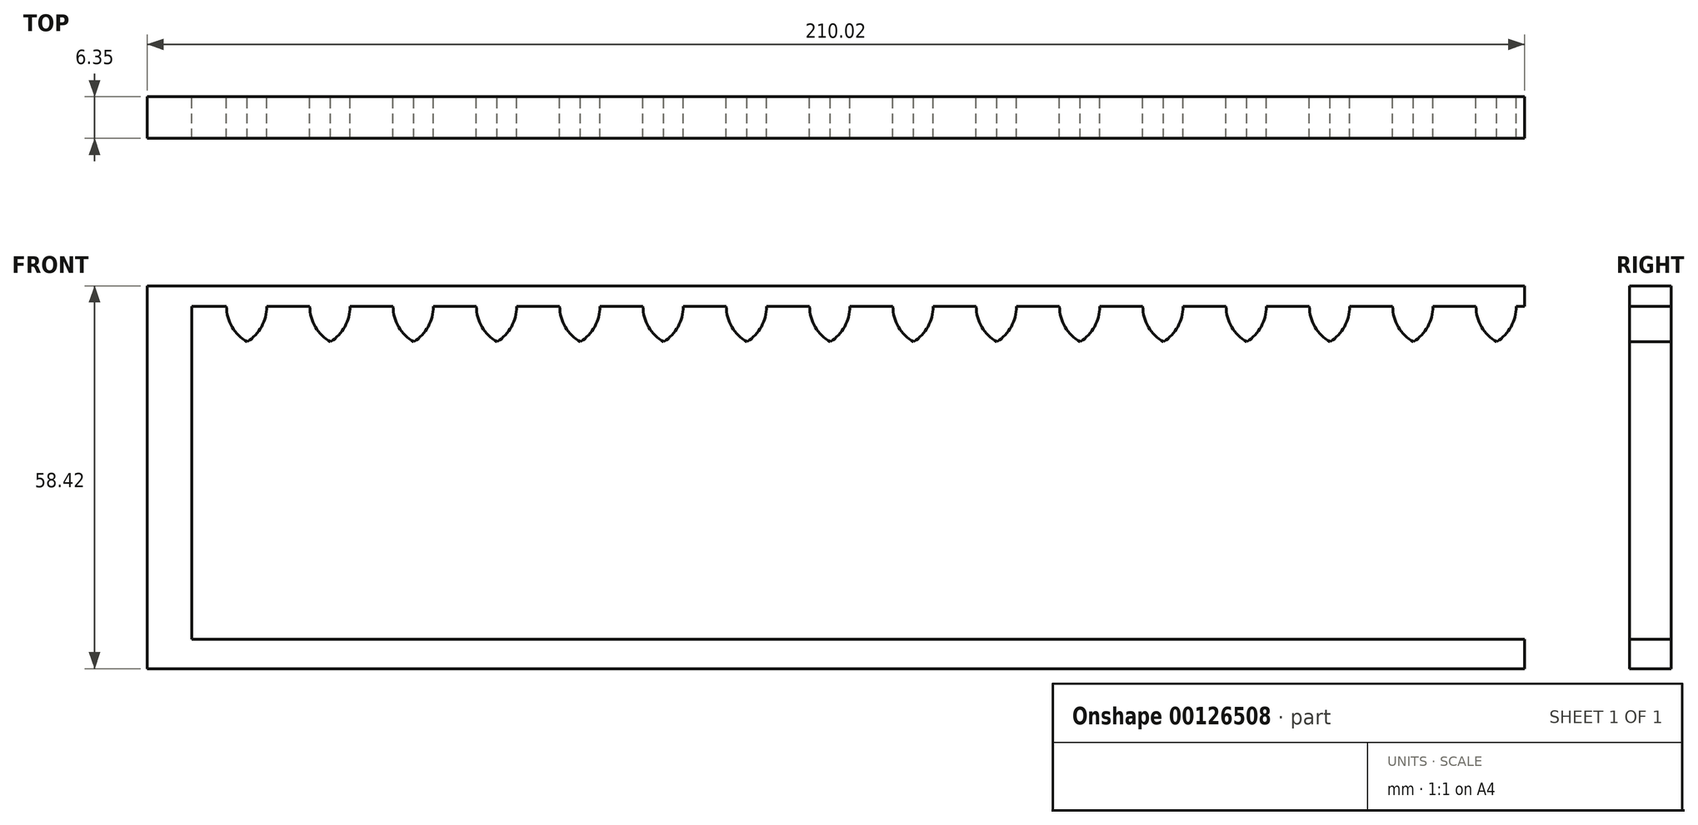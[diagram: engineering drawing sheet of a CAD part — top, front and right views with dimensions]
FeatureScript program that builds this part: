
annotation { "Feature Type Name" : "Feature", "Feature Type Description" : "" }
export const myFeature = defineFeature(function(context is Context, id is Id, definition is map)
    precondition{}
    {
        {
            var Q0;
            Q0=qCreatedBy(makeId("Front.planeOp"),FACE);
            var sketch = newSketch(context, id + "F0", { "sketchPlane" : qUnion([Q0])});
            skLineSegment(sketch, "E0.bottom", {"start": v(-100.17, 36.3) * mm, "end": v(103.03, 36.3) * mm});
            skLineSegment(sketch, "E0.top", {"start": v(-100.17, -14.5) * mm, "end": v(103.03, -14.5) * mm});
            skLineSegment(sketch, "E0.left", {"start": v(-100.17, 36.3) * mm, "end": v(-100.17, -14.5) * mm});
            skArc(sketch, "E1", {"start": v(-91.7, 30.93) * mm, "mid": v(-89.52, 33.23) * mm, "end": v(-88.73, 36.3) * mm});
            skArc(sketch, "E2", {"start": v(-94.87, 36.3) * mm, "mid": v(-94.02, 33.18) * mm, "end": v(-91.7, 30.93) * mm});
            skArc(sketch, "E3.1.0.0", {"start": v(-79, 30.93) * mm, "mid": v(-76.82, 33.23) * mm, "end": v(-76.03, 36.3) * mm});
            skArc(sketch, "E3.1.0.1", {"start": v(-82.17, 36.3) * mm, "mid": v(-81.32, 33.18) * mm, "end": v(-79, 30.93) * mm});
            skArc(sketch, "E3.2.0.0", {"start": v(-66.3, 30.93) * mm, "mid": v(-64.12, 33.23) * mm, "end": v(-63.33, 36.3) * mm});
            skArc(sketch, "E3.2.0.1", {"start": v(-69.47, 36.3) * mm, "mid": v(-68.62, 33.18) * mm, "end": v(-66.3, 30.93) * mm});
            skArc(sketch, "E3.3.0.0", {"start": v(-53.6, 30.93) * mm, "mid": v(-51.42, 33.23) * mm, "end": v(-50.63, 36.3) * mm});
            skArc(sketch, "E3.3.0.1", {"start": v(-56.77, 36.3) * mm, "mid": v(-55.92, 33.18) * mm, "end": v(-53.6, 30.93) * mm});
            skArc(sketch, "E3.4.0.0", {"start": v(-40.9, 30.93) * mm, "mid": v(-38.72, 33.23) * mm, "end": v(-37.93, 36.3) * mm});
            skArc(sketch, "E3.4.0.1", {"start": v(-44.07, 36.3) * mm, "mid": v(-43.22, 33.18) * mm, "end": v(-40.9, 30.93) * mm});
            skArc(sketch, "E3.5.0.0", {"start": v(-28.2, 30.93) * mm, "mid": v(-26.02, 33.23) * mm, "end": v(-25.23, 36.3) * mm});
            skArc(sketch, "E3.5.0.1", {"start": v(-31.37, 36.3) * mm, "mid": v(-30.52, 33.18) * mm, "end": v(-28.2, 30.93) * mm});
            skArc(sketch, "E3.6.0.0", {"start": v(-15.5, 30.93) * mm, "mid": v(-13.32, 33.23) * mm, "end": v(-12.53, 36.3) * mm});
            skArc(sketch, "E3.6.0.1", {"start": v(-18.67, 36.3) * mm, "mid": v(-17.82, 33.18) * mm, "end": v(-15.5, 30.93) * mm});
            skArc(sketch, "E3.7.0.0", {"start": v(-2.8, 30.93) * mm, "mid": v(-0.62, 33.23) * mm, "end": v(0.17, 36.3) * mm});
            skArc(sketch, "E3.7.0.1", {"start": v(-5.97, 36.3) * mm, "mid": v(-5.12, 33.18) * mm, "end": v(-2.8, 30.93) * mm});
            skArc(sketch, "E3.8.0.0", {"start": v(9.9, 30.93) * mm, "mid": v(12.08, 33.23) * mm, "end": v(12.87, 36.3) * mm});
            skArc(sketch, "E3.8.0.1", {"start": v(6.73, 36.3) * mm, "mid": v(7.58, 33.18) * mm, "end": v(9.9, 30.93) * mm});
            skArc(sketch, "E3.9.0.0", {"start": v(22.6, 30.93) * mm, "mid": v(24.78, 33.23) * mm, "end": v(25.57, 36.3) * mm});
            skArc(sketch, "E3.9.0.1", {"start": v(19.43, 36.3) * mm, "mid": v(20.28, 33.18) * mm, "end": v(22.6, 30.93) * mm});
            skArc(sketch, "E3.10.0.0", {"start": v(35.3, 30.93) * mm, "mid": v(37.48, 33.23) * mm, "end": v(38.27, 36.3) * mm});
            skArc(sketch, "E3.10.0.1", {"start": v(32.13, 36.3) * mm, "mid": v(32.98, 33.18) * mm, "end": v(35.3, 30.93) * mm});
            skArc(sketch, "E3.11.0.0", {"start": v(48, 30.93) * mm, "mid": v(50.18, 33.23) * mm, "end": v(50.97, 36.3) * mm});
            skArc(sketch, "E3.11.0.1", {"start": v(44.83, 36.3) * mm, "mid": v(45.68, 33.18) * mm, "end": v(48, 30.93) * mm});
            skArc(sketch, "E3.12.0.0", {"start": v(60.7, 30.93) * mm, "mid": v(62.88, 33.23) * mm, "end": v(63.67, 36.3) * mm});
            skArc(sketch, "E3.12.0.1", {"start": v(57.53, 36.3) * mm, "mid": v(58.38, 33.18) * mm, "end": v(60.7, 30.93) * mm});
            skArc(sketch, "E3.13.0.0", {"start": v(73.4, 30.93) * mm, "mid": v(75.58, 33.23) * mm, "end": v(76.37, 36.3) * mm});
            skArc(sketch, "E3.13.0.1", {"start": v(70.23, 36.3) * mm, "mid": v(71.08, 33.18) * mm, "end": v(73.4, 30.93) * mm});
            skArc(sketch, "E3.14.0.0", {"start": v(86.1, 30.93) * mm, "mid": v(88.28, 33.23) * mm, "end": v(89.07, 36.3) * mm});
            skArc(sketch, "E3.14.0.1", {"start": v(82.93, 36.3) * mm, "mid": v(83.78, 33.18) * mm, "end": v(86.1, 30.93) * mm});
            skArc(sketch, "E3.15.0.0", {"start": v(98.8, 30.93) * mm, "mid": v(100.98, 33.23) * mm, "end": v(101.77, 36.3) * mm});
            skArc(sketch, "E3.15.0.1", {"start": v(95.63, 36.3) * mm, "mid": v(96.48, 33.18) * mm, "end": v(98.8, 30.93) * mm});
            skLineSegment(sketch, "E3.direction1", {"start": v(-91.7, 30.93) * mm, "end": v(-79, 30.93) * mm, "construction": true});
            skArc(sketch, "E4.MirrorCS", {"start": v(-94.87, -14.5) * mm, "mid": v(-94.02, -11.38) * mm, "end": v(-91.7, -9.13) * mm});
            skArc(sketch, "E5.MirrorCS", {"start": v(-91.7, -9.13) * mm, "mid": v(-89.52, -11.43) * mm, "end": v(-88.73, -14.5) * mm});
            skArc(sketch, "E6.MirrorCS", {"start": v(-82.17, -14.5) * mm, "mid": v(-81.32, -11.38) * mm, "end": v(-79, -9.13) * mm});
            skArc(sketch, "E7.MirrorCS", {"start": v(-79, -9.13) * mm, "mid": v(-76.82, -11.43) * mm, "end": v(-76.03, -14.5) * mm});
            skArc(sketch, "E8.MirrorCS", {"start": v(-69.47, -14.5) * mm, "mid": v(-68.62, -11.38) * mm, "end": v(-66.3, -9.13) * mm});
            skArc(sketch, "E9.MirrorCS", {"start": v(-66.3, -9.13) * mm, "mid": v(-64.12, -11.43) * mm, "end": v(-63.33, -14.5) * mm});
            skArc(sketch, "E10.MirrorCS", {"start": v(-56.77, -14.5) * mm, "mid": v(-55.92, -11.38) * mm, "end": v(-53.6, -9.13) * mm});
            skArc(sketch, "E11.MirrorCS", {"start": v(-53.6, -9.13) * mm, "mid": v(-51.42, -11.43) * mm, "end": v(-50.63, -14.5) * mm});
            skArc(sketch, "E12.MirrorCS", {"start": v(-44.07, -14.5) * mm, "mid": v(-43.22, -11.38) * mm, "end": v(-40.9, -9.13) * mm});
            skArc(sketch, "E13.MirrorCS", {"start": v(-40.9, -9.13) * mm, "mid": v(-38.72, -11.43) * mm, "end": v(-37.93, -14.5) * mm});
            skArc(sketch, "E14.MirrorCS", {"start": v(-31.37, -14.5) * mm, "mid": v(-30.52, -11.38) * mm, "end": v(-28.2, -9.13) * mm});
            skArc(sketch, "E15.MirrorCS", {"start": v(-28.2, -9.13) * mm, "mid": v(-26.02, -11.43) * mm, "end": v(-25.23, -14.5) * mm});
            skArc(sketch, "E16.MirrorCS", {"start": v(-18.67, -14.5) * mm, "mid": v(-17.82, -11.38) * mm, "end": v(-15.5, -9.13) * mm});
            skArc(sketch, "E17.MirrorCS", {"start": v(-15.5, -9.13) * mm, "mid": v(-13.32, -11.43) * mm, "end": v(-12.53, -14.5) * mm});
            skArc(sketch, "E18.MirrorCS", {"start": v(-5.97, -14.5) * mm, "mid": v(-5.12, -11.38) * mm, "end": v(-2.8, -9.13) * mm});
            skArc(sketch, "E19.MirrorCS", {"start": v(-2.8, -9.13) * mm, "mid": v(-0.62, -11.43) * mm, "end": v(0.17, -14.5) * mm});
            skArc(sketch, "E20.MirrorCS", {"start": v(6.73, -14.5) * mm, "mid": v(7.58, -11.38) * mm, "end": v(9.9, -9.13) * mm});
            skArc(sketch, "E21.MirrorCS", {"start": v(9.9, -9.13) * mm, "mid": v(12.08, -11.43) * mm, "end": v(12.87, -14.5) * mm});
            skArc(sketch, "E22.MirrorCS", {"start": v(19.43, -14.5) * mm, "mid": v(20.28, -11.38) * mm, "end": v(22.6, -9.13) * mm});
            skArc(sketch, "E23.MirrorCS", {"start": v(22.6, -9.13) * mm, "mid": v(24.78, -11.43) * mm, "end": v(25.57, -14.5) * mm});
            skArc(sketch, "E24.MirrorCS", {"start": v(32.13, -14.5) * mm, "mid": v(32.98, -11.38) * mm, "end": v(35.3, -9.13) * mm});
            skArc(sketch, "E25.MirrorCS", {"start": v(35.3, -9.13) * mm, "mid": v(37.48, -11.43) * mm, "end": v(38.27, -14.5) * mm});
            skArc(sketch, "E26.MirrorCS", {"start": v(44.83, -14.5) * mm, "mid": v(45.68, -11.38) * mm, "end": v(48, -9.13) * mm});
            skArc(sketch, "E27.MirrorCS", {"start": v(48, -9.13) * mm, "mid": v(50.18, -11.43) * mm, "end": v(50.97, -14.5) * mm});
            skArc(sketch, "E28.MirrorCS", {"start": v(57.53, -14.5) * mm, "mid": v(58.38, -11.38) * mm, "end": v(60.7, -9.13) * mm});
            skArc(sketch, "E29.MirrorCS", {"start": v(60.7, -9.13) * mm, "mid": v(62.88, -11.43) * mm, "end": v(63.67, -14.5) * mm});
            skArc(sketch, "E30.MirrorCS", {"start": v(70.23, -14.5) * mm, "mid": v(71.08, -11.38) * mm, "end": v(73.4, -9.13) * mm});
            skArc(sketch, "E31.MirrorCS", {"start": v(73.4, -9.13) * mm, "mid": v(75.58, -11.43) * mm, "end": v(76.37, -14.5) * mm});
            skArc(sketch, "E32.MirrorCS", {"start": v(82.93, -14.5) * mm, "mid": v(83.78, -11.38) * mm, "end": v(86.1, -9.13) * mm});
            skArc(sketch, "E33.MirrorCS", {"start": v(86.1, -9.13) * mm, "mid": v(88.28, -11.43) * mm, "end": v(89.07, -14.5) * mm});
            skArc(sketch, "E34.MirrorCS", {"start": v(95.63, -14.5) * mm, "mid": v(96.48, -11.38) * mm, "end": v(98.8, -9.13) * mm});
            skArc(sketch, "E35.MirrorCS", {"start": v(98.8, -9.13) * mm, "mid": v(100.98, -11.43) * mm, "end": v(101.77, -14.5) * mm});
            skLineSegment(sketch, "E36.bottom", {"start": v(-107, 39.46) * mm, "end": v(103.03, 39.46) * mm});
            skLineSegment(sketch, "E36.top", {"start": v(-107, -18.96) * mm, "end": v(103.03, -18.96) * mm});
            skLineSegment(sketch, "E36.left", {"start": v(-107, 39.46) * mm, "end": v(-107, -18.96) * mm});
            skLineSegment(sketch, "E37", {"start": v(103.03, 36.3) * mm, "end": v(103.03, 39.46) * mm});
            skLineSegment(sketch, "E38", {"start": v(103.03, -14.5) * mm, "end": v(103.03, -18.96) * mm});
            skSolve(sketch);
        }
        {
            var Q0;
            {var subQ30=sQuery(id+"F0.wireOp",EDGE,"E0.left");Q0=makeQuery(id+"F0.imprint","IMPRINT",FACE,{"disambiguationData":[TD([[makeQuery(id+"F0.imprint","IMPRINT",EDGE,{"derivedFrom":subQ30}),-1.0]])]});}
            var Q1;
            {var subQ0=sQuery(id+"F0.wireOp",EDGE,"E1");Q1=makeQuery(id+"F0.imprint","IMPRINT",FACE,{"disambiguationData":[TD([[makeQuery(id+"F0.imprint","IMPRINT",EDGE,{"derivedFrom":subQ0}),1.0]])]});}
            var Q2;
            {var subQ0=sQuery(id+"F0.wireOp",EDGE,"E3.1.0.0");Q2=makeQuery(id+"F0.imprint","IMPRINT",FACE,{"disambiguationData":[TD([[makeQuery(id+"F0.imprint","IMPRINT",EDGE,{"derivedFrom":subQ0}),1.0]])]});}
            var Q3;
            {var subQ0=sQuery(id+"F0.wireOp",EDGE,"E3.2.0.0");Q3=makeQuery(id+"F0.imprint","IMPRINT",FACE,{"disambiguationData":[TD([[makeQuery(id+"F0.imprint","IMPRINT",EDGE,{"derivedFrom":subQ0}),1.0]])]});}
            var Q4;
            {var subQ0=sQuery(id+"F0.wireOp",EDGE,"E3.3.0.0");Q4=makeQuery(id+"F0.imprint","IMPRINT",FACE,{"disambiguationData":[TD([[makeQuery(id+"F0.imprint","IMPRINT",EDGE,{"derivedFrom":subQ0}),1.0]])]});}
            var Q5;
            {var subQ0=sQuery(id+"F0.wireOp",EDGE,"E3.4.0.0");Q5=makeQuery(id+"F0.imprint","IMPRINT",FACE,{"disambiguationData":[TD([[makeQuery(id+"F0.imprint","IMPRINT",EDGE,{"derivedFrom":subQ0}),1.0]])]});}
            var Q6;
            {var subQ0=sQuery(id+"F0.wireOp",EDGE,"E3.5.0.0");Q6=makeQuery(id+"F0.imprint","IMPRINT",FACE,{"disambiguationData":[TD([[makeQuery(id+"F0.imprint","IMPRINT",EDGE,{"derivedFrom":subQ0}),1.0]])]});}
            var Q7;
            {var subQ0=sQuery(id+"F0.wireOp",EDGE,"E3.6.0.0");Q7=makeQuery(id+"F0.imprint","IMPRINT",FACE,{"disambiguationData":[TD([[makeQuery(id+"F0.imprint","IMPRINT",EDGE,{"derivedFrom":subQ0}),1.0]])]});}
            var Q8;
            {var subQ0=sQuery(id+"F0.wireOp",EDGE,"E3.7.0.0");Q8=makeQuery(id+"F0.imprint","IMPRINT",FACE,{"disambiguationData":[TD([[makeQuery(id+"F0.imprint","IMPRINT",EDGE,{"derivedFrom":subQ0}),1.0]])]});}
            var Q9;
            {var subQ0=sQuery(id+"F0.wireOp",EDGE,"E3.8.0.0");Q9=makeQuery(id+"F0.imprint","IMPRINT",FACE,{"disambiguationData":[TD([[makeQuery(id+"F0.imprint","IMPRINT",EDGE,{"derivedFrom":subQ0}),1.0]])]});}
            var Q10;
            {var subQ0=sQuery(id+"F0.wireOp",EDGE,"E3.9.0.0");Q10=makeQuery(id+"F0.imprint","IMPRINT",FACE,{"disambiguationData":[TD([[makeQuery(id+"F0.imprint","IMPRINT",EDGE,{"derivedFrom":subQ0}),1.0]])]});}
            var Q11;
            {var subQ0=sQuery(id+"F0.wireOp",EDGE,"E3.10.0.0");Q11=makeQuery(id+"F0.imprint","IMPRINT",FACE,{"disambiguationData":[TD([[makeQuery(id+"F0.imprint","IMPRINT",EDGE,{"derivedFrom":subQ0}),1.0]])]});}
            var Q12;
            {var subQ0=sQuery(id+"F0.wireOp",EDGE,"E3.11.0.0");Q12=makeQuery(id+"F0.imprint","IMPRINT",FACE,{"disambiguationData":[TD([[makeQuery(id+"F0.imprint","IMPRINT",EDGE,{"derivedFrom":subQ0}),1.0]])]});}
            var Q13;
            {var subQ0=sQuery(id+"F0.wireOp",EDGE,"E3.12.0.0");Q13=makeQuery(id+"F0.imprint","IMPRINT",FACE,{"disambiguationData":[TD([[makeQuery(id+"F0.imprint","IMPRINT",EDGE,{"derivedFrom":subQ0}),1.0]])]});}
            var Q14;
            {var subQ0=sQuery(id+"F0.wireOp",EDGE,"E3.13.0.0");Q14=makeQuery(id+"F0.imprint","IMPRINT",FACE,{"disambiguationData":[TD([[makeQuery(id+"F0.imprint","IMPRINT",EDGE,{"derivedFrom":subQ0}),1.0]])]});}
            var Q15;
            {var subQ0=sQuery(id+"F0.wireOp",EDGE,"E3.14.0.0");Q15=makeQuery(id+"F0.imprint","IMPRINT",FACE,{"disambiguationData":[TD([[makeQuery(id+"F0.imprint","IMPRINT",EDGE,{"derivedFrom":subQ0}),1.0]])]});}
            var Q16;
            {var subQ0=sQuery(id+"F0.wireOp",EDGE,"E3.15.0.0");Q16=makeQuery(id+"F0.imprint","IMPRINT",FACE,{"disambiguationData":[TD([[makeQuery(id+"F0.imprint","IMPRINT",EDGE,{"derivedFrom":subQ0}),1.0]])]});}
            var Q17;
            {var subQ0=sQuery(id+"F0.wireOp",EDGE,"E34.MirrorCS");Q17=makeQuery(id+"F0.imprint","IMPRINT",FACE,{"disambiguationData":[TD([[makeQuery(id+"F0.imprint","IMPRINT",EDGE,{"derivedFrom":subQ0}),-1.0]])]});}
            var Q18;
            {var subQ0=sQuery(id+"F0.wireOp",EDGE,"E32.MirrorCS");Q18=makeQuery(id+"F0.imprint","IMPRINT",FACE,{"disambiguationData":[TD([[makeQuery(id+"F0.imprint","IMPRINT",EDGE,{"derivedFrom":subQ0}),-1.0]])]});}
            var Q19;
            {var subQ0=sQuery(id+"F0.wireOp",EDGE,"E30.MirrorCS");Q19=makeQuery(id+"F0.imprint","IMPRINT",FACE,{"disambiguationData":[TD([[makeQuery(id+"F0.imprint","IMPRINT",EDGE,{"derivedFrom":subQ0}),-1.0]])]});}
            var Q20;
            {var subQ0=sQuery(id+"F0.wireOp",EDGE,"E28.MirrorCS");Q20=makeQuery(id+"F0.imprint","IMPRINT",FACE,{"disambiguationData":[TD([[makeQuery(id+"F0.imprint","IMPRINT",EDGE,{"derivedFrom":subQ0}),-1.0]])]});}
            var Q21;
            {var subQ0=sQuery(id+"F0.wireOp",EDGE,"E26.MirrorCS");Q21=makeQuery(id+"F0.imprint","IMPRINT",FACE,{"disambiguationData":[TD([[makeQuery(id+"F0.imprint","IMPRINT",EDGE,{"derivedFrom":subQ0}),-1.0]])]});}
            var Q22;
            {var subQ0=sQuery(id+"F0.wireOp",EDGE,"E24.MirrorCS");Q22=makeQuery(id+"F0.imprint","IMPRINT",FACE,{"disambiguationData":[TD([[makeQuery(id+"F0.imprint","IMPRINT",EDGE,{"derivedFrom":subQ0}),-1.0]])]});}
            var Q23;
            {var subQ0=sQuery(id+"F0.wireOp",EDGE,"E22.MirrorCS");Q23=makeQuery(id+"F0.imprint","IMPRINT",FACE,{"disambiguationData":[TD([[makeQuery(id+"F0.imprint","IMPRINT",EDGE,{"derivedFrom":subQ0}),-1.0]])]});}
            var Q24;
            {var subQ0=sQuery(id+"F0.wireOp",EDGE,"E20.MirrorCS");Q24=makeQuery(id+"F0.imprint","IMPRINT",FACE,{"disambiguationData":[TD([[makeQuery(id+"F0.imprint","IMPRINT",EDGE,{"derivedFrom":subQ0}),-1.0]])]});}
            var Q25;
            {var subQ0=sQuery(id+"F0.wireOp",EDGE,"E18.MirrorCS");Q25=makeQuery(id+"F0.imprint","IMPRINT",FACE,{"disambiguationData":[TD([[makeQuery(id+"F0.imprint","IMPRINT",EDGE,{"derivedFrom":subQ0}),-1.0]])]});}
            var Q26;
            {var subQ0=sQuery(id+"F0.wireOp",EDGE,"E16.MirrorCS");Q26=makeQuery(id+"F0.imprint","IMPRINT",FACE,{"disambiguationData":[TD([[makeQuery(id+"F0.imprint","IMPRINT",EDGE,{"derivedFrom":subQ0}),-1.0]])]});}
            var Q27;
            {var subQ0=sQuery(id+"F0.wireOp",EDGE,"E14.MirrorCS");Q27=makeQuery(id+"F0.imprint","IMPRINT",FACE,{"disambiguationData":[TD([[makeQuery(id+"F0.imprint","IMPRINT",EDGE,{"derivedFrom":subQ0}),-1.0]])]});}
            var Q28;
            {var subQ0=sQuery(id+"F0.wireOp",EDGE,"E12.MirrorCS");Q28=makeQuery(id+"F0.imprint","IMPRINT",FACE,{"disambiguationData":[TD([[makeQuery(id+"F0.imprint","IMPRINT",EDGE,{"derivedFrom":subQ0}),-1.0]])]});}
            var Q29;
            {var subQ0=sQuery(id+"F0.wireOp",EDGE,"E10.MirrorCS");Q29=makeQuery(id+"F0.imprint","IMPRINT",FACE,{"disambiguationData":[TD([[makeQuery(id+"F0.imprint","IMPRINT",EDGE,{"derivedFrom":subQ0}),-1.0]])]});}
            var Q30;
            {var subQ0=sQuery(id+"F0.wireOp",EDGE,"E8.MirrorCS");Q30=makeQuery(id+"F0.imprint","IMPRINT",FACE,{"disambiguationData":[TD([[makeQuery(id+"F0.imprint","IMPRINT",EDGE,{"derivedFrom":subQ0}),-1.0]])]});}
            var Q31;
            {var subQ0=sQuery(id+"F0.wireOp",EDGE,"E6.MirrorCS");Q31=makeQuery(id+"F0.imprint","IMPRINT",FACE,{"disambiguationData":[TD([[makeQuery(id+"F0.imprint","IMPRINT",EDGE,{"derivedFrom":subQ0}),-1.0]])]});}
            var Q32;
            {var subQ0=sQuery(id+"F0.wireOp",EDGE,"E4.MirrorCS");Q32=makeQuery(id+"F0.imprint","IMPRINT",FACE,{"disambiguationData":[TD([[makeQuery(id+"F0.imprint","IMPRINT",EDGE,{"derivedFrom":subQ0}),-1.0]])]});}
            extrude(context, id + "F1", {"entities" : qUnion([Q0, Q1, Q2, Q3, Q4, Q5, Q6, Q7, Q8, Q9, Q10, Q11, Q12, Q13, Q14, Q15, Q16, Q17, Q18, Q19, Q20, Q21, Q22, Q23, Q24, Q25, Q26, Q27, Q28, Q29, Q30, Q31, Q32]), "depth" : 6.35 * mm});
        }
        {
            var Q0;
            Q0=makeQuery(id+"F1.opExtrude","SWEPT_BODY",BODY,{"disambiguationData":[OSD([sQuery(id+"F0.wireOp",EDGE,"E0.bottom"),sQuery(id+"F0.wireOp",EDGE,"E0.top"),sQuery(id+"F0.wireOp",EDGE,"E0.left"),sQuery(id+"F0.wireOp",EDGE,"E1"),sQuery(id+"F0.wireOp",EDGE,"E2"),sQuery(id+"F0.wireOp",EDGE,"E3.1.0.0"),sQuery(id+"F0.wireOp",EDGE,"E3.1.0.1"),sQuery(id+"F0.wireOp",EDGE,"E3.2.0.0"),sQuery(id+"F0.wireOp",EDGE,"E3.2.0.1"),sQuery(id+"F0.wireOp",EDGE,"E3.3.0.0"),sQuery(id+"F0.wireOp",EDGE,"E3.3.0.1"),sQuery(id+"F0.wireOp",EDGE,"E3.4.0.0"),sQuery(id+"F0.wireOp",EDGE,"E3.4.0.1"),sQuery(id+"F0.wireOp",EDGE,"E3.5.0.0"),sQuery(id+"F0.wireOp",EDGE,"E3.5.0.1"),sQuery(id+"F0.wireOp",EDGE,"E3.6.0.0"),sQuery(id+"F0.wireOp",EDGE,"E3.6.0.1"),sQuery(id+"F0.wireOp",EDGE,"E3.7.0.0"),sQuery(id+"F0.wireOp",EDGE,"E3.7.0.1"),sQuery(id+"F0.wireOp",EDGE,"E3.8.0.0"),sQuery(id+"F0.wireOp",EDGE,"E3.8.0.1"),sQuery(id+"F0.wireOp",EDGE,"E3.9.0.0"),sQuery(id+"F0.wireOp",EDGE,"E3.9.0.1"),sQuery(id+"F0.wireOp",EDGE,"E3.10.0.0"),sQuery(id+"F0.wireOp",EDGE,"E3.10.0.1"),sQuery(id+"F0.wireOp",EDGE,"E3.11.0.0"),sQuery(id+"F0.wireOp",EDGE,"E3.11.0.1"),sQuery(id+"F0.wireOp",EDGE,"E3.12.0.0"),sQuery(id+"F0.wireOp",EDGE,"E3.12.0.1"),sQuery(id+"F0.wireOp",EDGE,"E3.13.0.0"),sQuery(id+"F0.wireOp",EDGE,"E3.13.0.1"),sQuery(id+"F0.wireOp",EDGE,"E3.14.0.0"),sQuery(id+"F0.wireOp",EDGE,"E3.14.0.1"),sQuery(id+"F0.wireOp",EDGE,"E3.15.0.0"),sQuery(id+"F0.wireOp",EDGE,"E3.15.0.1"),sQuery(id+"F0.wireOp",EDGE,"E4.MirrorCS"),sQuery(id+"F0.wireOp",EDGE,"E5.MirrorCS"),sQuery(id+"F0.wireOp",EDGE,"E6.MirrorCS"),sQuery(id+"F0.wireOp",EDGE,"E7.MirrorCS"),sQuery(id+"F0.wireOp",EDGE,"E8.MirrorCS"),sQuery(id+"F0.wireOp",EDGE,"E9.MirrorCS"),sQuery(id+"F0.wireOp",EDGE,"E10.MirrorCS"),sQuery(id+"F0.wireOp",EDGE,"E11.MirrorCS"),sQuery(id+"F0.wireOp",EDGE,"E12.MirrorCS"),sQuery(id+"F0.wireOp",EDGE,"E13.MirrorCS"),sQuery(id+"F0.wireOp",EDGE,"E14.MirrorCS"),sQuery(id+"F0.wireOp",EDGE,"E15.MirrorCS"),sQuery(id+"F0.wireOp",EDGE,"E16.MirrorCS"),sQuery(id+"F0.wireOp",EDGE,"E17.MirrorCS"),sQuery(id+"F0.wireOp",EDGE,"E18.MirrorCS"),sQuery(id+"F0.wireOp",EDGE,"E19.MirrorCS"),sQuery(id+"F0.wireOp",EDGE,"E20.MirrorCS"),sQuery(id+"F0.wireOp",EDGE,"E21.MirrorCS"),sQuery(id+"F0.wireOp",EDGE,"E22.MirrorCS"),sQuery(id+"F0.wireOp",EDGE,"E23.MirrorCS"),sQuery(id+"F0.wireOp",EDGE,"E24.MirrorCS"),sQuery(id+"F0.wireOp",EDGE,"E25.MirrorCS"),sQuery(id+"F0.wireOp",EDGE,"E26.MirrorCS"),sQuery(id+"F0.wireOp",EDGE,"E27.MirrorCS"),sQuery(id+"F0.wireOp",EDGE,"E28.MirrorCS"),sQuery(id+"F0.wireOp",EDGE,"E29.MirrorCS"),sQuery(id+"F0.wireOp",EDGE,"E30.MirrorCS"),sQuery(id+"F0.wireOp",EDGE,"E31.MirrorCS"),sQuery(id+"F0.wireOp",EDGE,"E32.MirrorCS"),sQuery(id+"F0.wireOp",EDGE,"E33.MirrorCS"),sQuery(id+"F0.wireOp",EDGE,"E34.MirrorCS"),sQuery(id+"F0.wireOp",EDGE,"E35.MirrorCS"),sQuery(id+"F0.wireOp",EDGE,"E36.bottom"),sQuery(id+"F0.wireOp",EDGE,"E36.top"),sQuery(id+"F0.wireOp",EDGE,"E36.left"),sQuery(id+"F0.wireOp",EDGE,"E37"),sQuery(id+"F0.wireOp",EDGE,"E38")])]});
            transform(context, id + "F2", {"entities" : qUnion([Q0]), "transformType" : TransformType.TRANSLATION_3D, "dx" : 0 * mm, "dy" : 0 * mm, "dz" : 0 * mm, "makeCopy" : true});
        }
    });
